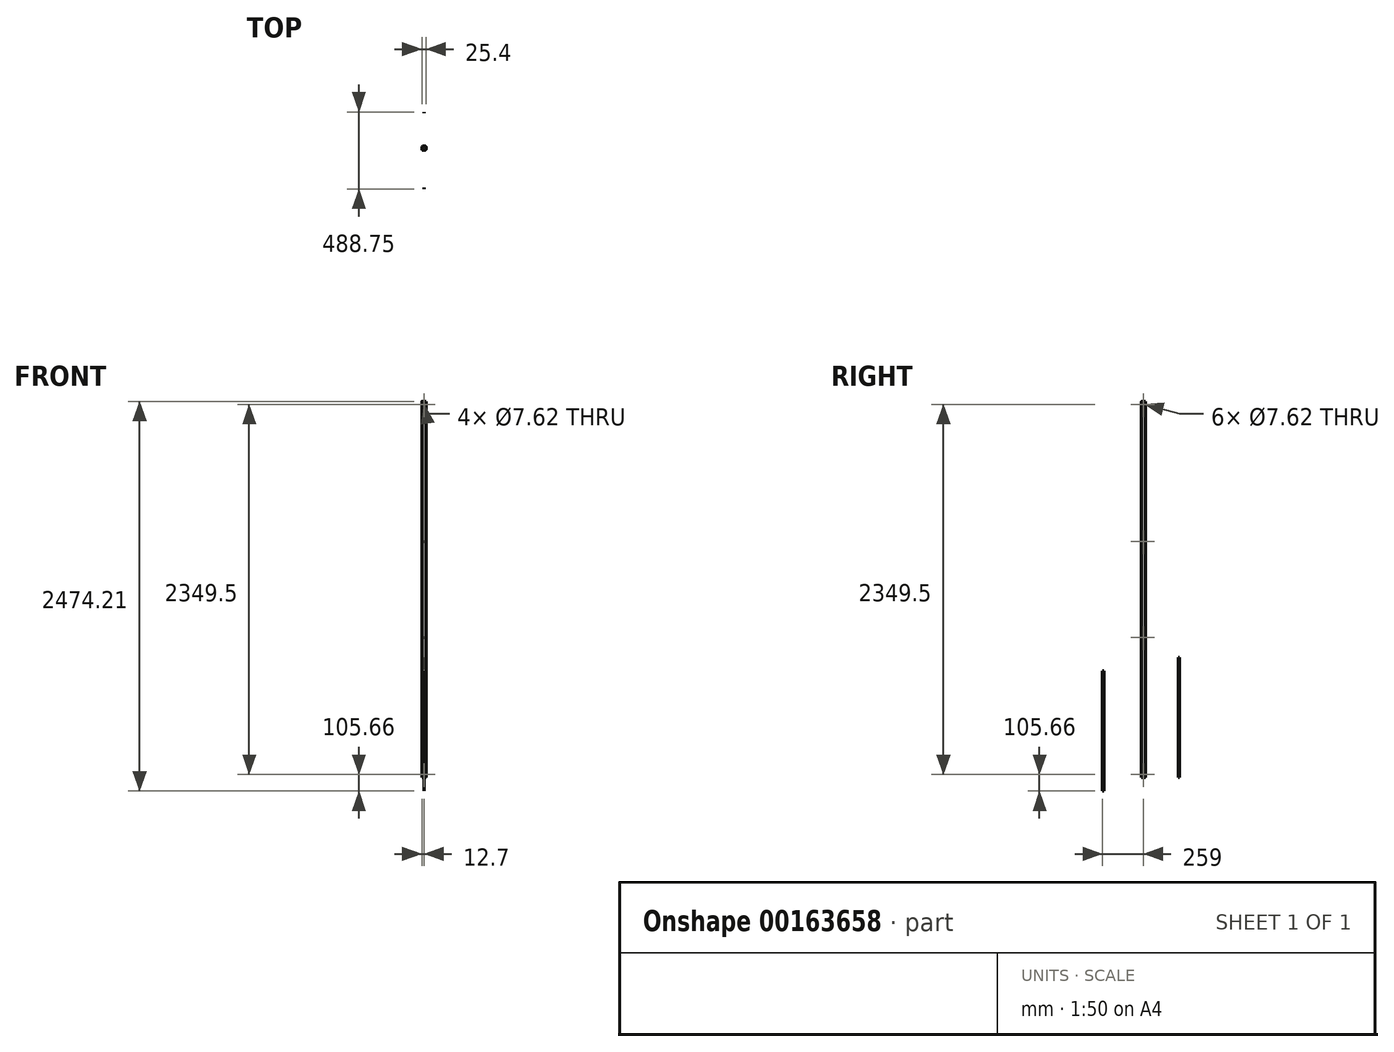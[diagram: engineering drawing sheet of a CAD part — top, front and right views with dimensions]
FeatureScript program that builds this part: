
annotation { "Feature Type Name" : "Feature", "Feature Type Description" : "" }
export const myFeature = defineFeature(function(context is Context, id is Id, definition is map)
    precondition{}
    {
        {
            var Q0;
            Q0=qCreatedBy(makeId("Top.planeOp"),FACE);
            var sketch = newSketch(context, id + "F0", { "sketchPlane" : qUnion([Q0])});
            skLineSegment(sketch, "E0.bottom", {"start": v(6.35, 12.7) * mm, "end": v(-6.35, 12.7) * mm});
            skLineSegment(sketch, "E0.top", {"start": v(6.35, -12.7) * mm, "end": v(-6.35, -12.7) * mm});
            skLineSegment(sketch, "E0.left", {"start": v(12.7, 6.35) * mm, "end": v(12.7, -6.35) * mm});
            skLineSegment(sketch, "E0.right", {"start": v(-12.7, 6.35) * mm, "end": v(-12.7, -6.35) * mm});
            skPoint(sketch, "E0.middle", {"position": v(0, 0) * mm});
            skPoint(sketch, "E1.visualSharp", {"position": v(-12.7, 12.7) * mm});
            skArc(sketch, "E1.filletArc", {"start": v(-6.35, 12.7) * mm, "mid": v(-10.84, 10.84) * mm, "end": v(-12.7, 6.35) * mm});
            skPoint(sketch, "E2.visualSharp", {"position": v(-12.7, -12.7) * mm});
            skArc(sketch, "E2.filletArc", {"start": v(-12.7, -6.35) * mm, "mid": v(-10.84, -10.84) * mm, "end": v(-6.35, -12.7) * mm});
            skPoint(sketch, "E3.visualSharp", {"position": v(12.7, -12.7) * mm});
            skArc(sketch, "E3.filletArc", {"start": v(6.35, -12.7) * mm, "mid": v(10.84, -10.84) * mm, "end": v(12.7, -6.35) * mm});
            skPoint(sketch, "E4.visualSharp", {"position": v(12.7, 12.7) * mm});
            skArc(sketch, "E4.filletArc", {"start": v(12.7, 6.35) * mm, "mid": v(10.84, 10.84) * mm, "end": v(6.35, 12.7) * mm});
            skSolve(sketch);
        }
        {
            var Q0;
            Q0=qSketchRegion(id+"F0",true);
            extrude(context, id + "F1", {"entities" : qUnion([Q0]), "depth" : 2387.6 * mm});
        }
        {
            var Q0;
            Q0=qCreatedBy(makeId("Right.planeOp"),FACE);
            var sketch = newSketch(context, id + "F2", { "sketchPlane" : qUnion([Q0])});
            skLineSegment(sketch, "E5.bottom", {"start": v(-259, 675.39) * mm, "end": v(-250.53, 675.39) * mm});
            skLineSegment(sketch, "E5.top", {"start": v(-259, -86.61) * mm, "end": v(-250.53, -86.61) * mm});
            skLineSegment(sketch, "E5.left", {"start": v(-259, 675.39) * mm, "end": v(-259, -86.61) * mm});
            skLineSegment(sketch, "E5.right", {"start": v(-250.53, 675.39) * mm, "end": v(-250.53, -86.61) * mm});
            skSolve(sketch);
        }
        {
            var Q0;
            Q0=makeQuery(id+"F2.imprint","IMPRINT",FACE,{"disambiguationData":[TD([[makeQuery(id+"F2.imprint","IMPRINT",EDGE,{"derivedFrom":sQuery(id+"F2.wireOp",EDGE,"E5.bottom")}),-1.0]])]});
            extrude(context, id + "F3", {"entities" : qUnion([Q0]), "depth" : 1.27 * mm});
        }
        {
            var Q0;
            Q0=qCreatedBy(makeId("Right.planeOp"),FACE);
            var sketch = newSketch(context, id + "F4", { "sketchPlane" : qUnion([Q0])});
            skLineSegment(sketch, "E6.bottom", {"start": v(221.29, 762) * mm, "end": v(229.75, 762) * mm});
            skLineSegment(sketch, "E6.top", {"start": v(221.29, 0) * mm, "end": v(229.75, 0) * mm});
            skLineSegment(sketch, "E6.left", {"start": v(221.29, 762) * mm, "end": v(221.29, 0) * mm});
            skLineSegment(sketch, "E6.right", {"start": v(229.75, 762) * mm, "end": v(229.75, 0) * mm});
            skSolve(sketch);
        }
        {
            var Q0;
            Q0=makeQuery(id+"F4.imprint","IMPRINT",FACE,{"disambiguationData":[TD([[makeQuery(id+"F4.imprint","IMPRINT",EDGE,{"derivedFrom":sQuery(id+"F4.wireOp",EDGE,"E6.bottom")}),-1.0]])]});
            var Q1;
            Q1=sQuery(id+"F4.wireOp",EDGE,"E6.right");
            var Q2;
            Q2=sQuery(id+"F4.wireOp",EDGE,"E6.left");
            var Q3;
            Q3=sQuery(id+"F4.wireOp",EDGE,"E6.top");
            var Q4;
            Q4=sQuery(id+"F4.wireOp",EDGE,"E6.bottom");
            extrude(context, id + "F5", {"entities" : qUnion([Q0]), "surfaceEntities" : qUnion([Q1, Q2, Q3, Q4]), "depth" : 1.27 * mm});
        }
        {
            var Q0;
            Q0=makeQuery(id+"F1.opExtrude","SWEPT_FACE",FACE,{"disambiguationData":[OSD([sQuery(id+"F0.wireOp",EDGE,"E0.top")])]});
            var sketch = newSketch(context, id + "F6", { "sketchPlane" : qUnion([Q0])});
            skLineSegment(sketch, "E7", {"start": v(0, 2387.6) * mm, "end": v(0, 2368.55) * mm});
            skPoint(sketch, "E7.endSnap0", {"position": v(0, 2387.6) * mm});
            skCircle(sketch, "E8", {"center": v(0, 2368.55) * mm, "radius": 3.81 * mm});
            skLineSegment(sketch, "E9", {"start": v(0, 0) * mm, "end": v(0, 19.05) * mm});
            skCircle(sketch, "E10", {"center": v(0, 19.05) * mm, "radius": 3.81 * mm});
            skSolve(sketch);
        }
        {
            var Q0;
            Q0=makeQuery(id+"F6.imprint","IMPRINT",FACE,{"disambiguationData":[TD([[makeQuery(id+"F6.imprint","IMPRINT",EDGE,{"derivedFrom":sQuery(id+"F6.wireOp",EDGE,"E8")}),1.0]])]});
            extrude(context, id + "F7", {"entities" : qUnion([Q0]), "operationType" : NewBodyOperationType.REMOVE, "oppositeDirection" : true, "depth" : 25.4 * mm});
        }
        {
            var Q0;
            Q0=qSketchRegion(id+"F6",true);
            extrude(context, id + "F8", {"entities" : qUnion([Q0]), "operationType" : NewBodyOperationType.REMOVE, "oppositeDirection" : true, "depth" : 25.4 * mm});
        }
        {
            var Q0;
            Q0=makeQuery(id+"F1.opExtrude","SWEPT_FACE",FACE,{"disambiguationData":[OSD([sQuery(id+"F0.wireOp",EDGE,"E0.left")])]});
            var sketch = newSketch(context, id + "F9", { "sketchPlane" : qUnion([Q0])});
            skLineSegment(sketch, "E11", {"start": v(0, 0) * mm, "end": v(0, 19.05) * mm});
            skPoint(sketch, "E11.endSnap0", {"position": v(0, 0) * mm});
            skCircle(sketch, "E12", {"center": v(0, 19.05) * mm, "radius": 3.81 * mm});
            skLineSegment(sketch, "E13", {"start": v(0, 2387.6) * mm, "end": v(0, 2368.55) * mm});
            skPoint(sketch, "E13.endSnap0", {"position": v(0, 2387.6) * mm});
            skCircle(sketch, "E14", {"center": v(0, 2368.55) * mm, "radius": 3.81 * mm});
            skSolve(sketch);
        }
        {
            var Q0;
            Q0=makeQuery(id+"F9.imprint","IMPRINT",FACE,{"disambiguationData":[TD([[makeQuery(id+"F9.imprint","IMPRINT",EDGE,{"derivedFrom":sQuery(id+"F9.wireOp",EDGE,"E14")}),1.0]])]});
            var Q1;
            Q1=makeQuery(id+"F9.imprint","IMPRINT",FACE,{"disambiguationData":[TD([[makeQuery(id+"F9.imprint","IMPRINT",EDGE,{"derivedFrom":sQuery(id+"F9.wireOp",EDGE,"E12")}),1.0]])]});
            extrude(context, id + "F10", {"entities" : qUnion([Q0, Q1]), "operationType" : NewBodyOperationType.REMOVE, "oppositeDirection" : true, "depth" : 25.4 * mm});
        }
        {
            var Q0;
            Q0=makeQuery(id+"F1.opExtrude","SWEPT_FACE",FACE,{"disambiguationData":[OSD([sQuery(id+"F0.wireOp",EDGE,"E0.left")])]});
            var sketch = newSketch(context, id + "F11", { "sketchPlane" : qUnion([Q0])});
            skLineSegment(sketch, "E15", {"start": v(6.35, 1193.8) * mm, "end": v(-6.35, 1193.8) * mm});
            skPoint(sketch, "E16.endSnap0", {"position": v(0, 1193.8) * mm});
            skCircle(sketch, "E17", {"center": v(0, 889) * mm, "radius": 3.81 * mm});
            skCircle(sketch, "E18", {"center": v(0, 1498.6) * mm, "radius": 3.81 * mm});
            skSolve(sketch);
        }
        {
            var Q0;
            Q0=makeQuery(id+"F11.imprint","IMPRINT",FACE,{"disambiguationData":[TD([[makeQuery(id+"F11.imprint","IMPRINT",EDGE,{"derivedFrom":sQuery(id+"F11.wireOp",EDGE,"E17")}),1.0]])]});
            var Q1;
            Q1=makeQuery(id+"F11.imprint","IMPRINT",FACE,{"disambiguationData":[TD([[makeQuery(id+"F11.imprint","IMPRINT",EDGE,{"derivedFrom":sQuery(id+"F11.wireOp",EDGE,"E18")}),1.0]])]});
            extrude(context, id + "F12", {"entities" : qUnion([Q0, Q1]), "operationType" : NewBodyOperationType.REMOVE, "oppositeDirection" : true, "depth" : 25.4 * mm});
        }
    });
